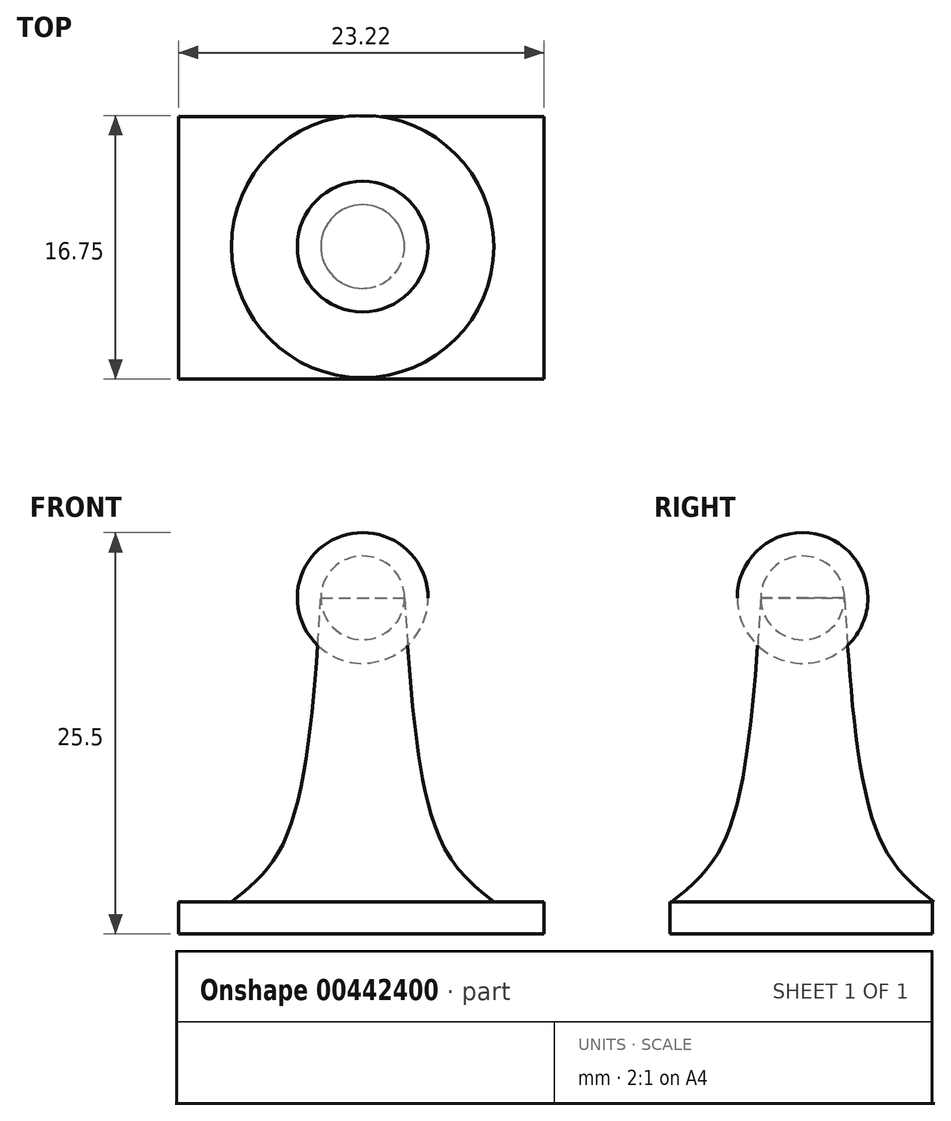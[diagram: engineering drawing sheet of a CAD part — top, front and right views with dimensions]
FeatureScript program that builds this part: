
annotation { "Feature Type Name" : "Feature", "Feature Type Description" : "" }
export const myFeature = defineFeature(function(context is Context, id is Id, definition is map)
    precondition{}
    {
        {
            var Q0;
            Q0=qCreatedBy(makeId("Top.planeOp"),FACE);
            var sketch = newSketch(context, id + "F0", { "sketchPlane" : qUnion([Q0])});
            skLineSegment(sketch, "E0.bottom", {"start": v(-11.7, 8.24) * mm, "end": v(11.52, 8.24) * mm});
            skLineSegment(sketch, "E0.top", {"start": v(-11.7, -8.42) * mm, "end": v(11.52, -8.42) * mm});
            skLineSegment(sketch, "E0.left", {"start": v(-11.7, 8.24) * mm, "end": v(-11.7, -8.42) * mm});
            skLineSegment(sketch, "E0.right", {"start": v(11.52, 8.24) * mm, "end": v(11.52, -8.42) * mm});
            skSolve(sketch);
        }
        {
            var Q0;
            Q0 = qSketchRegion(id + "F0", true);
            extrude(context, id + "F1", {"entities" : qUnion([Q0]), "depth" : 2.03 * mm});
        }
        {
            var Q0;
            Q0=qCreatedBy(makeId("Right.planeOp"),FACE);
            var sketch = newSketch(context, id + "F2", { "sketchPlane" : qUnion([Q0])});
            skFitSpline(sketch, "E1", {"points": [v(-8.33, 2.04) * mm, v(-4.96, 5.94) * mm, v(-2.66, 21.35) * mm], "startDerivative": vector(10.25, 8.2) * mm, "endDerivative": vector(1.85, 28.6) * mm});
            skFitSpline(sketch, "E2", {"points": [v(-2.66, 21.35) * mm, v(0, 21.35) * mm], "startDerivative": vector(2.66, 0) * mm, "endDerivative": vector(2.66, 0) * mm});
            skLineSegment(sketch, "E3", {"start": v(-8.33, 2.04) * mm, "end": v(0, 2.04) * mm});
            skLineSegment(sketch, "E4", {"start": v(0, 2.04) * mm, "end": v(0, 21.35) * mm});
            skSolve(sketch);
        }
        {
            var Q0;
            Q0=makeQuery(id+"F2.imprint","IMPRINT",FACE,{"disambiguationData":[TD([[makeQuery(id+"F2.imprint","IMPRINT",EDGE,{"derivedFrom":sQuery(id+"F2.wireOp",EDGE,"E1")}),-1.0]])]});
            var Q1;
            Q1=sQuery(id+"F2.wireOp",EDGE,"E4");
            revolve(context, id + "F3", {"entities" : qUnion([Q0]), "axis" : qUnion([Q1]), "revolveType" : RevolveType.FULL});
        }
        {
            var Q0;
            Q0=makeQuery(id+"F3.opRevolve","SWEPT_FACE",FACE,{"disambiguationData":[OSD([sQuery(id+"F2.wireOp",EDGE,"E2")])]});
            var sketch = newSketch(context, id + "F4", { "sketchPlane" : qUnion([Q0])});
            skCircle(sketch, "E5", {"center": v(0, 0) * mm, "radius": 4.15 * mm});
            skLineSegment(sketch, "E6", {"start": v(0, 4.15) * mm, "end": v(0, -4.15) * mm});
            skSolve(sketch);
        }
        {
            var Q0;
            {var subQ0=sQuery(id+"F4.wireOp",EDGE,"E6");var subQ1=sQuery(id+"F4.wireOp",EDGE,"E5");var subQ2=makeQuery(id+"F4.imprint","INTERSECT",VERTEX,{"disambiguationData":[OD(0.0)],"derivedFrom":[subQ1,subQ0]});Q0=makeQuery(id+"F4.imprint","IMPRINT",FACE,{"disambiguationData":[TD([[makeQuery(id+"F4.imprint","IMPRINT",EDGE,{"disambiguationData":[TD([[subQ2,-1.0]])],"derivedFrom":subQ1}),1.0]])]});}
            var Q1;
            Q1=sQuery(id+"F4.wireOp",EDGE,"E5");
            var Q2;
            Q2=sQuery(id+"F4.wireOp",EDGE,"E6");
            revolve(context, id + "F5", {"entities" : qUnion([Q0]), "surfaceEntities" : qUnion([Q1]), "axis" : qUnion([Q2]), "revolveType" : RevolveType.FULL});
        }
    });
